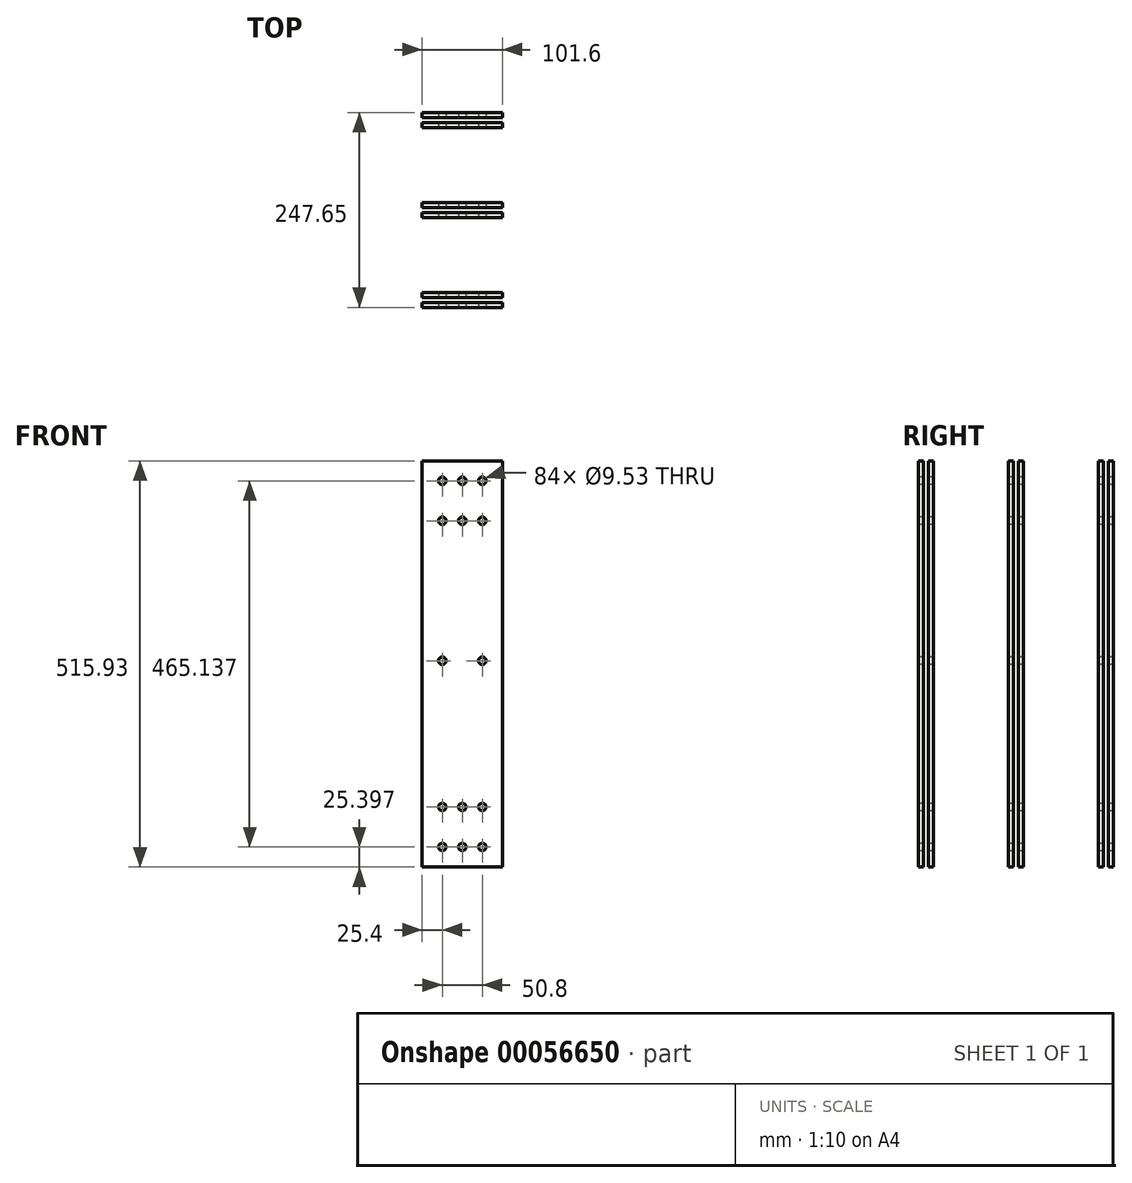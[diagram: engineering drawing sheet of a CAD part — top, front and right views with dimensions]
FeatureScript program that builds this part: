
annotation { "Feature Type Name" : "Feature", "Feature Type Description" : "" }
export const myFeature = defineFeature(function(context is Context, id is Id, definition is map)
    precondition{}
    {
        {
            var Q0;
            Q0=qCreatedBy(makeId("Right.planeOp"),FACE);
            var sketch = newSketch(context, id + "F0", { "sketchPlane" : qUnion([Q0])});
            skLineSegment(sketch, "E0.bottom", {"start": v(-38.9, 272.35) * mm, "end": v(-32.55, 272.35) * mm});
            skLineSegment(sketch, "E0.top", {"start": v(-38.9, -243.58) * mm, "end": v(-32.55, -243.58) * mm});
            skLineSegment(sketch, "E0.left", {"start": v(-38.9, 272.35) * mm, "end": v(-38.9, -243.58) * mm});
            skLineSegment(sketch, "E0.right", {"start": v(-32.55, 272.35) * mm, "end": v(-32.55, -243.58) * mm});
            skLineSegment(sketch, "E1.1.0.0", {"start": v(-26.2, 272.35) * mm, "end": v(-26.2, -243.58) * mm});
            skLineSegment(sketch, "E1.1.0.1", {"start": v(-19.85, 272.35) * mm, "end": v(-19.85, -243.58) * mm});
            skLineSegment(sketch, "E1.1.0.2", {"start": v(-26.2, 272.35) * mm, "end": v(-19.85, 272.35) * mm});
            skLineSegment(sketch, "E1.1.0.3", {"start": v(-26.2, -243.58) * mm, "end": v(-19.85, -243.58) * mm});
            skLineSegment(sketch, "E1.direction1", {"start": v(-38.9, -243.58) * mm, "end": v(-26.2, -243.58) * mm, "construction": true});
            skLineSegment(sketch, "E2.1.0.0", {"start": v(75.4, 272.35) * mm, "end": v(75.4, -243.58) * mm});
            skLineSegment(sketch, "E2.1.0.1", {"start": v(81.75, 272.35) * mm, "end": v(81.75, -243.58) * mm});
            skLineSegment(sketch, "E2.1.0.2", {"start": v(88.1, 272.35) * mm, "end": v(88.1, -243.58) * mm});
            skLineSegment(sketch, "E2.1.0.3", {"start": v(94.45, 272.35) * mm, "end": v(94.45, -243.58) * mm});
            skLineSegment(sketch, "E2.1.0.4", {"start": v(88.1, 272.35) * mm, "end": v(94.45, 272.35) * mm});
            skLineSegment(sketch, "E2.1.0.5", {"start": v(75.4, -243.58) * mm, "end": v(81.75, -243.58) * mm});
            skLineSegment(sketch, "E2.1.0.6", {"start": v(88.1, -243.58) * mm, "end": v(94.45, -243.58) * mm});
            skLineSegment(sketch, "E2.1.0.7", {"start": v(75.4, -243.58) * mm, "end": v(88.1, -243.58) * mm, "construction": true});
            skLineSegment(sketch, "E2.1.0.8", {"start": v(75.4, 272.35) * mm, "end": v(81.75, 272.35) * mm});
            skLineSegment(sketch, "E2.2.0.0", {"start": v(189.7, 272.35) * mm, "end": v(189.7, -243.58) * mm});
            skLineSegment(sketch, "E2.2.0.1", {"start": v(196.05, 272.35) * mm, "end": v(196.05, -243.58) * mm});
            skLineSegment(sketch, "E2.2.0.2", {"start": v(202.4, 272.35) * mm, "end": v(202.4, -243.58) * mm});
            skLineSegment(sketch, "E2.2.0.3", {"start": v(208.75, 272.35) * mm, "end": v(208.75, -243.58) * mm});
            skLineSegment(sketch, "E2.2.0.4", {"start": v(202.4, 272.35) * mm, "end": v(208.75, 272.35) * mm});
            skLineSegment(sketch, "E2.2.0.5", {"start": v(189.7, -243.58) * mm, "end": v(196.05, -243.58) * mm});
            skLineSegment(sketch, "E2.2.0.6", {"start": v(202.4, -243.58) * mm, "end": v(208.75, -243.58) * mm});
            skLineSegment(sketch, "E2.2.0.7", {"start": v(189.7, -243.58) * mm, "end": v(202.4, -243.58) * mm, "construction": true});
            skLineSegment(sketch, "E2.2.0.8", {"start": v(189.7, 272.35) * mm, "end": v(196.05, 272.35) * mm});
            skLineSegment(sketch, "E2.direction1", {"start": v(-38.9, -243.58) * mm, "end": v(75.4, -243.58) * mm, "construction": true});
            skSolve(sketch);
        }
        {
            var Q0;
            Q0 = qSketchRegion(id + "F0", true);
            extrude(context, id + "F1", {"entities" : qUnion([Q0]), "endBound" : BoundingType.SYMMETRIC, "depth" : 101.6 * mm});
        }
        {
            var Q0;
            Q0=makeQuery(id+"F1.opExtrude","SWEPT_FACE",FACE,{"disambiguationData":[OSD([sQuery(id+"F0.wireOp",EDGE,"E0.left")])]});
            var sketch = newSketch(context, id + "F2", { "sketchPlane" : qUnion([Q0])});
            skCircle(sketch, "E3", {"center": v(-25.4, 246.95) * mm, "radius": 4.76 * mm});
            skCircle(sketch, "E4", {"center": v(-25.4, -218.18) * mm, "radius": 4.76 * mm});
            skCircle(sketch, "E5.0.1.0", {"center": v(-25.4, 196.15) * mm, "radius": 4.76 * mm});
            skCircle(sketch, "E5.1.0.0", {"center": v(0, 246.95) * mm, "radius": 4.76 * mm});
            skCircle(sketch, "E5.1.1.0", {"center": v(0, 196.15) * mm, "radius": 4.76 * mm});
            skCircle(sketch, "E5.2.0.0", {"center": v(25.4, 246.95) * mm, "radius": 4.76 * mm});
            skCircle(sketch, "E5.2.1.0", {"center": v(25.4, 196.15) * mm, "radius": 4.76 * mm});
            skLineSegment(sketch, "E5.direction1", {"start": v(-25.4, 246.95) * mm, "end": v(0, 246.95) * mm, "construction": true});
            skLineSegment(sketch, "E5.direction2", {"start": v(-25.4, 246.95) * mm, "end": v(-25.4, 196.15) * mm, "construction": true});
            skCircle(sketch, "E6.0.1.0", {"center": v(-25.4, -167.38) * mm, "radius": 4.76 * mm});
            skCircle(sketch, "E6.1.0.0", {"center": v(0, -218.18) * mm, "radius": 4.76 * mm});
            skCircle(sketch, "E6.1.1.0", {"center": v(0, -167.38) * mm, "radius": 4.76 * mm});
            skCircle(sketch, "E6.2.0.0", {"center": v(25.4, -218.18) * mm, "radius": 4.76 * mm});
            skCircle(sketch, "E6.2.1.0", {"center": v(25.4, -167.38) * mm, "radius": 4.76 * mm});
            skLineSegment(sketch, "E6.direction1", {"start": v(-25.4, -218.18) * mm, "end": v(0, -218.18) * mm, "construction": true});
            skLineSegment(sketch, "E6.direction2", {"start": v(-25.4, -218.18) * mm, "end": v(-25.4, -167.38) * mm, "construction": true});
            skCircle(sketch, "E7", {"center": v(25.4, 18.35) * mm, "radius": 4.76 * mm});
            skCircle(sketch, "E8", {"center": v(-25.4, 18.35) * mm, "radius": 4.76 * mm});
            skSolve(sketch);
        }
        {
            var Q0;
            Q0 = qSketchRegion(id + "F2", true);
            extrude(context, id + "F3", {"entities" : qUnion([Q0]), "operationType" : NewBodyOperationType.REMOVE, "endBound" : BoundingType.THROUGH_ALL, "oppositeDirection" : true, "depth" : 25.4 * mm});
        }
    });
